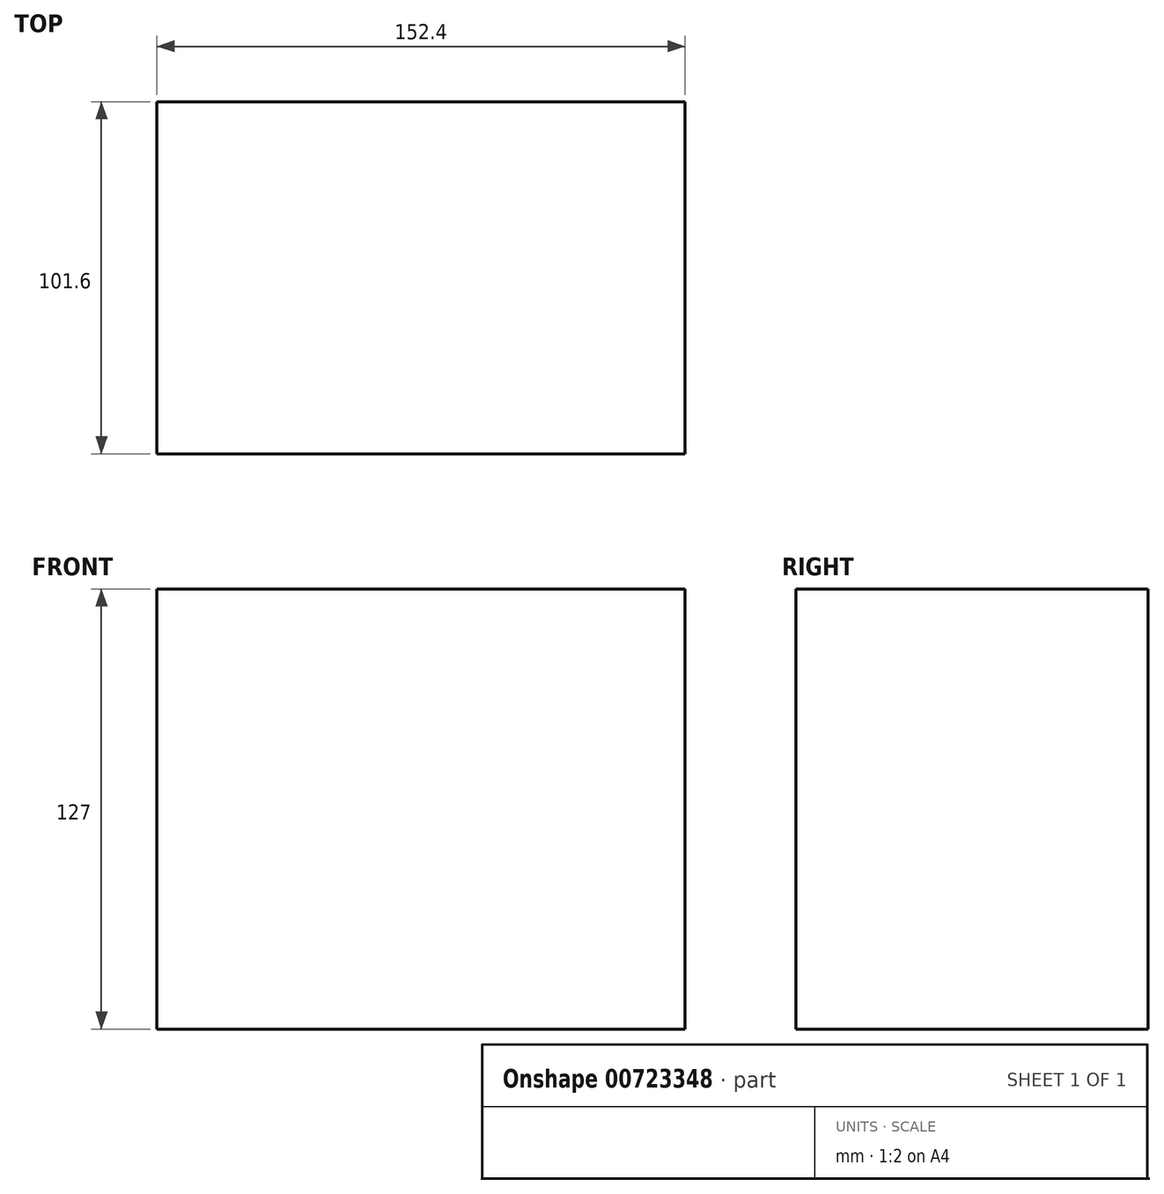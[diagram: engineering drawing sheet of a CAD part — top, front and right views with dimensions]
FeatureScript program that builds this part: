
annotation { "Feature Type Name" : "Feature", "Feature Type Description" : "" }
export const myFeature = defineFeature(function(context is Context, id is Id, definition is map)
    precondition{}
    {
        {
            var Q0;
            Q0=qCreatedBy(makeId("Front.planeOp"),FACE);
            var sketch = newSketch(context, id + "F0", { "sketchPlane" : qUnion([Q0])});
            skLineSegment(sketch, "E0", {"start": v(-95.74, -48.4) * mm, "end": v(-95.74, 78.6) * mm});
            skLineSegment(sketch, "E1", {"start": v(-95.74, 78.6) * mm, "end": v(56.66, 78.6) * mm});
            skLineSegment(sketch, "E2", {"start": v(56.66, 78.6) * mm, "end": v(56.66, -48.4) * mm});
            skLineSegment(sketch, "E3", {"start": v(56.66, -48.4) * mm, "end": v(-95.74, -48.4) * mm});
            skSolve(sketch);
        }
        {
            var Q0;
            Q0=makeQuery(id+"F0.imprint","IMPRINT",FACE,{"disambiguationData":[TD([[makeQuery(id+"F0.imprint","IMPRINT",EDGE,{"derivedFrom":sQuery(id+"F0.wireOp",EDGE,"E0")}),-1.0]])]});
            extrude(context, id + "F1", {"entities" : qUnion([Q0]), "depth" : 101.6 * mm, "offsetDistance" : 25.4 * mm});
        }
    });
